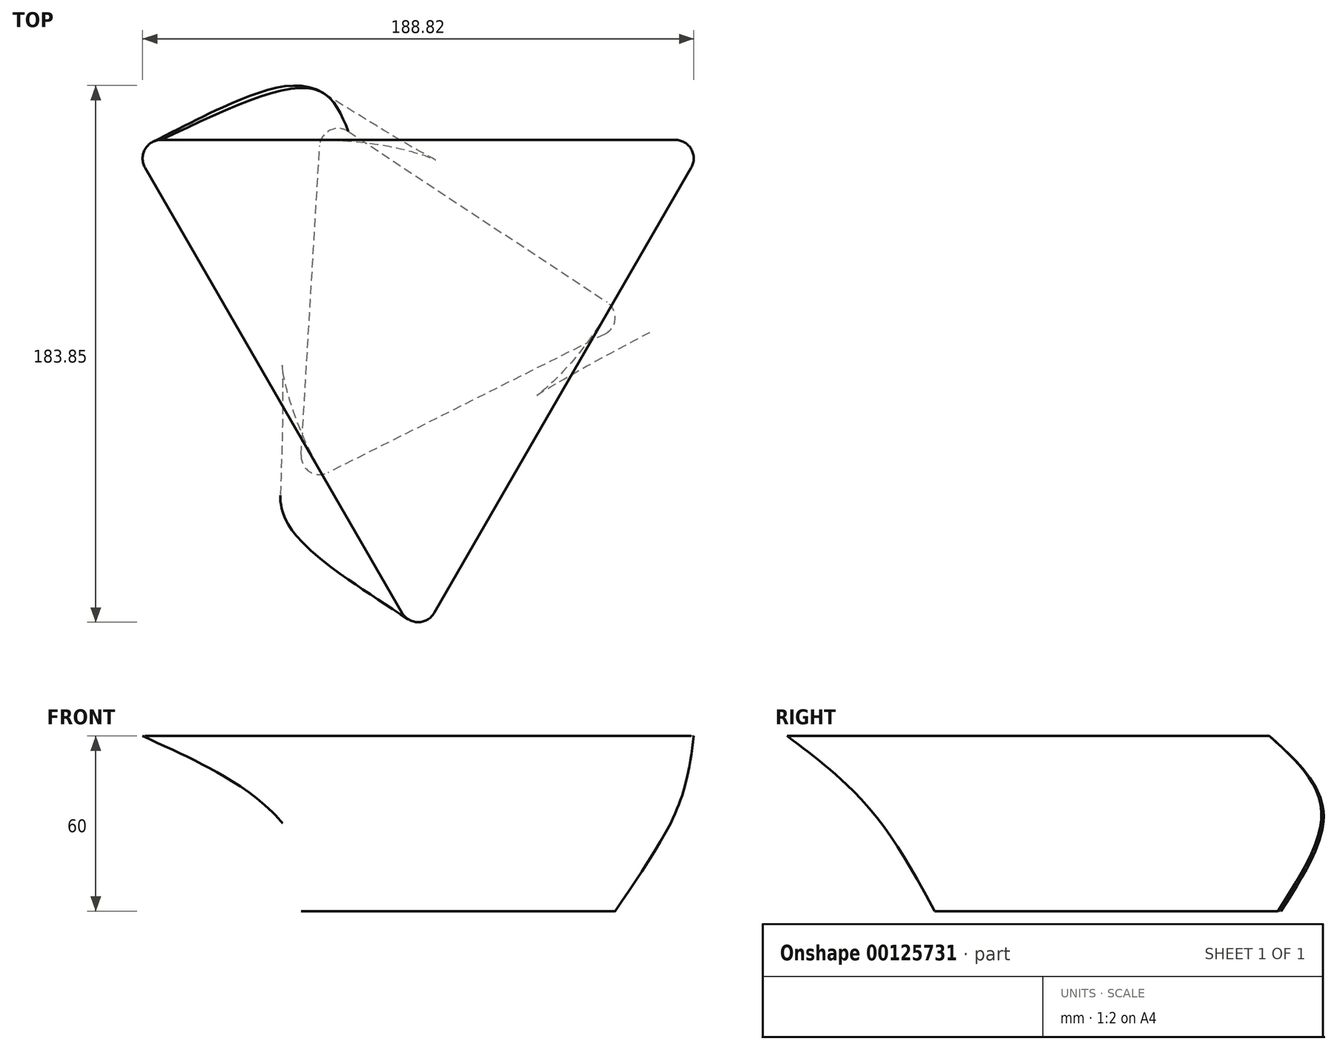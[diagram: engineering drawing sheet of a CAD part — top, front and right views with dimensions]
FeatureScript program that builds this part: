
annotation { "Feature Type Name" : "Feature", "Feature Type Description" : "" }
export const myFeature = defineFeature(function(context is Context, id is Id, definition is map)
    precondition{}
    {
        {
            var Q0;
            Q0=qCreatedBy(makeId("Top.planeOp"),FACE);
            cPlane(context, id + "F0", {"entities" : qUnion([Q0]), "cplaneType" : CPlaneType.OFFSET, "offset" : 30 * mm, "width" : 152.4 * mm, "height" : 152.4 * mm});
        }
        {
            var Q0;
            Q0=qCreatedBy(makeId("Top.planeOp"),FACE);
            cPlane(context, id + "F1", {"entities" : qUnion([Q0]), "cplaneType" : CPlaneType.OFFSET, "offset" : 60 * mm, "width" : 152.4 * mm, "height" : 152.4 * mm});
        }
        {
            var Q0;
            Q0=qCreatedBy(makeId("Top.planeOp"),FACE);
            var sketch = newSketch(context, id + "F2", { "sketchPlane" : qUnion([Q0])});
            skCircle(sketch, "E0.cCircle", {"center": v(0, 0) * mm, "radius": 36.98 * mm, "construction": true});
            skLineSegment(sketch, "E0.0", {"start": v(-23.92, 60.1) * mm, "end": v(64.66, 1.64) * mm});
            skLineSegment(sketch, "E0.1", {"start": v(64, -9.33) * mm, "end": v(-30.9, -56.82) * mm});
            skLineSegment(sketch, "E0.2", {"start": v(-40.08, -50.76) * mm, "end": v(-33.75, 55.17) * mm});
            skPoint(sketch, "E0.0.midPoint", {"position": v(20.37, 30.87) * mm});
            skPoint(sketch, "E1.visualSharp", {"position": v(-33.1, 66.15) * mm});
            skArc(sketch, "E1.filletArc", {"start": v(-23.92, 60.1) * mm, "mid": v(-30.25, 60.47) * mm, "end": v(-33.75, 55.17) * mm});
            skPoint(sketch, "E2.visualSharp", {"position": v(-40.74, -61.74) * mm});
            skArc(sketch, "E2.filletArc", {"start": v(-40.08, -50.76) * mm, "mid": v(-37.24, -56.44) * mm, "end": v(-30.9, -56.82) * mm});
            skPoint(sketch, "E3.visualSharp", {"position": v(73.84, -4.41) * mm});
            skArc(sketch, "E3.filletArc", {"start": v(64, -9.33) * mm, "mid": v(67.5, -4.03) * mm, "end": v(64.66, 1.64) * mm});
            skSolve(sketch);
        }
        {
            var Q0;
            Q0=qCreatedBy(id+"F0.planeOp",FACE);
            var sketch = newSketch(context, id + "F3", { "sketchPlane" : qUnion([Q0])});
            skCircle(sketch, "E4.cCircle", {"center": v(0, 0) * mm, "radius": 46.38 * mm, "construction": true});
            skLineSegment(sketch, "E4.0", {"start": v(-46.38, -69.34) * mm, "end": v(-46.38, 69.34) * mm});
            skLineSegment(sketch, "E4.1", {"start": v(-36.86, 74.84) * mm, "end": v(83.24, 5.5) * mm});
            skLineSegment(sketch, "E4.2", {"start": v(83.24, -5.5) * mm, "end": v(-36.86, -74.84) * mm});
            skPoint(sketch, "E4.0.midPoint", {"position": v(-46.38, 0) * mm});
            skPoint(sketch, "E5.visualSharp", {"position": v(-46.38, 80.34) * mm});
            skArc(sketch, "E5.filletArc", {"start": v(-36.86, 74.84) * mm, "mid": v(-43.2, 74.84) * mm, "end": v(-46.38, 69.34) * mm});
            skPoint(sketch, "E6.visualSharp", {"position": v(-46.38, -80.34) * mm});
            skArc(sketch, "E6.filletArc", {"start": v(-46.38, -69.34) * mm, "mid": v(-43.2, -74.84) * mm, "end": v(-36.86, -74.84) * mm});
            skPoint(sketch, "E7.visualSharp", {"position": v(92.76, 0) * mm});
            skArc(sketch, "E7.filletArc", {"start": v(83.24, -5.5) * mm, "mid": v(86.41, 0) * mm, "end": v(83.24, 5.5) * mm});
            skSolve(sketch);
        }
        {
            var Q0;
            Q0=qCreatedBy(id+"F1.planeOp",FACE);
            var sketch = newSketch(context, id + "F4", { "sketchPlane" : qUnion([Q0])});
            skCircle(sketch, "E8.cCircle", {"center": v(0, 0) * mm, "radius": 57.2 * mm, "construction": true});
            skLineSegment(sketch, "E8.0", {"start": v(-88.06, 57.2) * mm, "end": v(88.06, 57.2) * mm});
            skLineSegment(sketch, "E8.1", {"start": v(93.56, 47.67) * mm, "end": v(5.5, -104.86) * mm});
            skLineSegment(sketch, "E8.2", {"start": v(-5.5, -104.86) * mm, "end": v(-93.56, 47.67) * mm});
            skPoint(sketch, "E8.0.midPoint", {"position": v(0, 57.2) * mm});
            skPoint(sketch, "E9.visualSharp", {"position": v(-99.06, 57.2) * mm});
            skArc(sketch, "E9.filletArc", {"start": v(-88.06, 57.2) * mm, "mid": v(-93.56, 54.02) * mm, "end": v(-93.56, 47.67) * mm});
            skPoint(sketch, "E10.visualSharp", {"position": v(0, -114.39) * mm});
            skArc(sketch, "E10.filletArc", {"start": v(-5.5, -104.86) * mm, "mid": v(0, -108.04) * mm, "end": v(5.5, -104.86) * mm});
            skPoint(sketch, "E11.visualSharp", {"position": v(99.06, 57.2) * mm});
            skArc(sketch, "E11.filletArc", {"start": v(93.56, 47.67) * mm, "mid": v(93.56, 54.02) * mm, "end": v(88.06, 57.2) * mm});
            skSolve(sketch);
        }
        {
            var Q0;
            Q0=makeQuery(id+"F2.imprint","IMPRINT",FACE,{"disambiguationData":[TD([[makeQuery(id+"F2.imprint","IMPRINT",EDGE,{"derivedFrom":sQuery(id+"F2.wireOp",EDGE,"E0.0")}),-1.0]])]});
            var Q1;
            Q1=makeQuery(id+"F3.imprint","IMPRINT",FACE,{"disambiguationData":[TD([[makeQuery(id+"F3.imprint","IMPRINT",EDGE,{"derivedFrom":sQuery(id+"F3.wireOp",EDGE,"E4.0")}),-1.0]])]});
            var Q2;
            Q2=makeQuery(id+"F4.imprint","IMPRINT",FACE,{"disambiguationData":[TD([[makeQuery(id+"F4.imprint","IMPRINT",EDGE,{"derivedFrom":sQuery(id+"F4.wireOp",EDGE,"E8.0")}),-1.0]])]});
            loft(context, id + "F5", {"sheetProfilesArray" : [{ "sheetProfileEntities" : qUnion([Q0]) }, { "sheetProfileEntities" : qUnion([Q1]) }, { "sheetProfileEntities" : qUnion([Q2]) }]});
        }
    });
